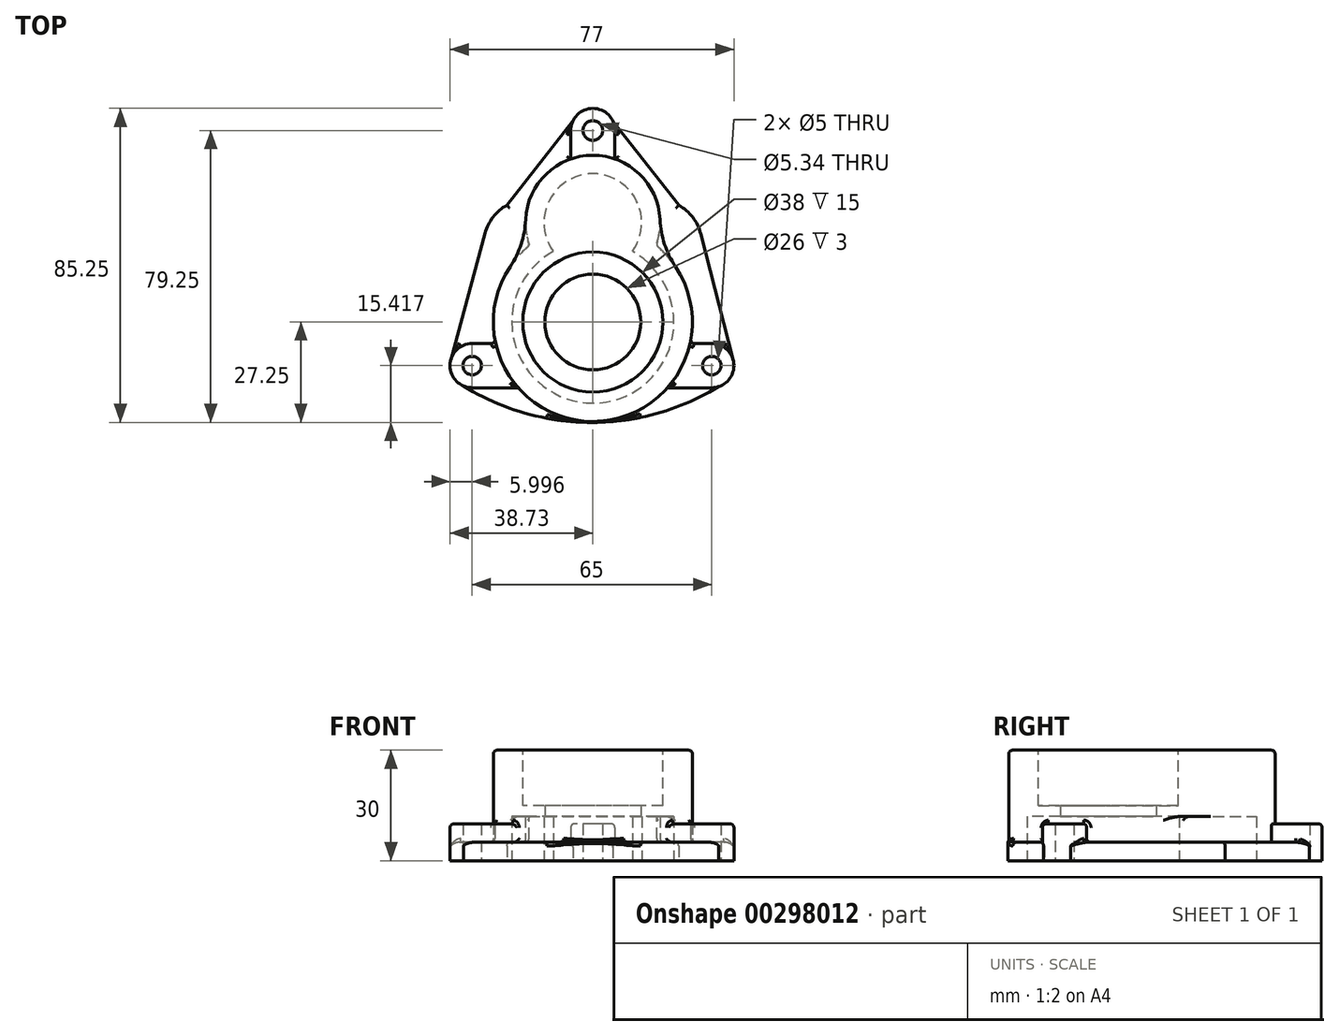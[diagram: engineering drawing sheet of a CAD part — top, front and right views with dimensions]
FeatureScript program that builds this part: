
annotation { "Feature Type Name" : "Feature", "Feature Type Description" : "" }
export const myFeature = defineFeature(function(context is Context, id is Id, definition is map)
    precondition{}
    {
        {
            var Q0;
            Q0=qCreatedBy(makeId("Top.planeOp"),FACE);
            var sketch = newSketch(context, id + "F0", { "sketchPlane" : qUnion([Q0])});
            skCircle(sketch, "E0", {"center": v(0, 0) * mm, "radius": 13 * mm});
            skCircle(sketch, "E1", {"center": v(0, 0) * mm, "radius": 22 * mm});
            skCircle(sketch, "E2", {"center": v(0, 0) * mm, "radius": 27 * mm});
            skCircle(sketch, "E3", {"center": v(0, 27) * mm, "radius": 13.26 * mm});
            skArc(sketch, "E4", {"start": v(17.18, 20.83) * mm, "mid": v(0, 45.26) * mm, "end": v(-17.18, 20.83) * mm});
            skCircle(sketch, "E5", {"center": v(0, 52) * mm, "radius": 2.67 * mm});
            skCircle(sketch, "E6", {"center": v(0, 52) * mm, "radius": 6 * mm});
            skLineSegment(sketch, "E7", {"start": v(-6, 52) * mm, "end": v(-6, 44.25) * mm});
            skLineSegment(sketch, "E8", {"start": v(6, 52) * mm, "end": v(6, 44.25) * mm});
            skCircle(sketch, "E9", {"center": v(32.27, -11.83) * mm, "radius": 2.5 * mm});
            skCircle(sketch, "E10", {"center": v(-32.73, -11.83) * mm, "radius": 2.5 * mm});
            skCircle(sketch, "E11", {"center": v(-32.73, -11.83) * mm, "radius": 6 * mm});
            skCircle(sketch, "E12", {"center": v(32.27, -11.83) * mm, "radius": 6 * mm});
            skLineSegment(sketch, "E13", {"start": v(-32.73, -5.83) * mm, "end": v(-26.36, -5.83) * mm});
            skLineSegment(sketch, "E14", {"start": v(-32.73, -17.83) * mm, "end": v(-20.27, -17.83) * mm});
            skLineSegment(sketch, "E15", {"start": v(32.27, -5.83) * mm, "end": v(26.36, -5.83) * mm});
            skLineSegment(sketch, "E16", {"start": v(32.27, -17.83) * mm, "end": v(20.27, -17.83) * mm});
            skArc(sketch, "E17", {"start": v(-0.52, 13.75) * mm, "mid": v(-0.33, 13.37) * mm, "end": v(-0.12, 13) * mm});
            skArc(sketch, "E18.trimOffspring", {"start": v(-0.1, 13) * mm, "mid": v(0, 13.37) * mm, "end": v(0.09, 13.74) * mm});
            skArc(sketch, "E19", {"start": v(-35.1, -17.35) * mm, "mid": v(-0.52, -27.25) * mm, "end": v(34.11, -17.54) * mm});
            skArc(sketch, "E20", {"start": v(-23.28, 31.74) * mm, "mid": v(-27.04, 28.51) * mm, "end": v(-29.25, 24.08) * mm});
            skArc(sketch, "E21", {"start": v(29.3, 23.93) * mm, "mid": v(27.1, 28.45) * mm, "end": v(23.28, 31.74) * mm});
            skLineSegment(sketch, "E22", {"start": v(5.4, 54.6) * mm, "end": v(23.28, 31.74) * mm});
            skLineSegment(sketch, "E23", {"start": v(-38.52, -10.23) * mm, "end": v(-29.25, 24.08) * mm});
            skLineSegment(sketch, "E24", {"start": v(38.05, -10.23) * mm, "end": v(29.25, 24.08) * mm});
            skLineSegment(sketch, "E25", {"start": v(-23.28, 31.74) * mm, "end": v(-5.4, 54.6) * mm});
            skCircle(sketch, "E26", {"center": v(0, 0) * mm, "radius": 19 * mm});
            skSolve(sketch);
        }
        {
            var Q0;
            {var subQ0=sQuery(id+"F0.wireOp",EDGE,"E4");var subQ1=sQuery(id+"F0.wireOp",EDGE,"E2");var subQ2=makeQuery(id+"F0.imprint","INTERSECT",VERTEX,{"disambiguationData":[OD(0.0)],"derivedFrom":[subQ1,subQ0]});Q0=makeQuery(id+"F0.imprint","IMPRINT",FACE,{"disambiguationData":[TD([[makeQuery(id+"F0.imprint","IMPRINT",EDGE,{"disambiguationData":[TD([[subQ2,-1.0]])],"derivedFrom":subQ1}),-1.0]])]});}
            var Q1;
            {var subQ0=sQuery(id+"F0.wireOp",EDGE,"E3");var subQ1=sQuery(id+"F0.wireOp",EDGE,"E2");var subQ2=makeQuery(id+"F0.imprint","INTERSECT",VERTEX,{"disambiguationData":[OD(0.0)],"derivedFrom":[subQ1,subQ0]});Q1=makeQuery(id+"F0.imprint","IMPRINT",FACE,{"disambiguationData":[TD([[makeQuery(id+"F0.imprint","IMPRINT",EDGE,{"disambiguationData":[TD([[subQ2,-1.0]])],"derivedFrom":subQ1}),-1.0]])]});}
            var Q2;
            {var subQ0=sQuery(id+"F0.wireOp",EDGE,"E3");var subQ1=sQuery(id+"F0.wireOp",EDGE,"E1");var subQ2=makeQuery(id+"F0.imprint","INTERSECT",VERTEX,{"disambiguationData":[OD(0.0)],"derivedFrom":[subQ1,subQ0]});Q2=makeQuery(id+"F0.imprint","IMPRINT",FACE,{"disambiguationData":[TD([[makeQuery(id+"F0.imprint","IMPRINT",EDGE,{"disambiguationData":[TD([[subQ2,1.0]])],"derivedFrom":subQ1}),-1.0]])]});}
            var Q3;
            {var subQ0=sQuery(id+"F0.wireOp",EDGE,"E3");var subQ1=sQuery(id+"F0.wireOp",EDGE,"E1");var subQ2=makeQuery(id+"F0.imprint","INTERSECT",VERTEX,{"disambiguationData":[OD(0.0)],"derivedFrom":[subQ1,subQ0]});Q3=makeQuery(id+"F0.imprint","IMPRINT",FACE,{"disambiguationData":[TD([[makeQuery(id+"F0.imprint","IMPRINT",EDGE,{"disambiguationData":[TD([[subQ2,1.0]])],"derivedFrom":subQ1}),1.0]])]});}
            var Q4;
            {var subQ5=sQuery(id+"F0.wireOp",EDGE,"E3");var subQ7=sQuery(id+"F0.wireOp",EDGE,"E1");var subQ8=makeQuery(id+"F0.imprint","INTERSECT",VERTEX,{"disambiguationData":[OD(0.0)],"derivedFrom":[subQ7,subQ5]});Q4=makeQuery(id+"F0.imprint","IMPRINT",FACE,{"disambiguationData":[TD([[makeQuery(id+"F0.imprint","IMPRINT",EDGE,{"disambiguationData":[TD([[subQ8,-1.0]])],"derivedFrom":subQ7}),-1.0]])]});}
            var Q5;
            {var subQ0=sQuery(id+"F0.wireOp",EDGE,"E17");Q5=makeQuery(id+"F0.imprint","IMPRINT",FACE,{"disambiguationData":[TD([[makeQuery(id+"F0.imprint","IMPRINT",EDGE,{"derivedFrom":subQ0}),-1.0]])]});}
            var Q6;
            {var subQ0=sQuery(id+"F0.wireOp",EDGE,"E0");var subQ1=makeQuery(id+"F0.imprint","INTERSECT",VERTEX,{"derivedFrom":[subQ0,sQuery(id+"F0.wireOp",EDGE,"E17")]});Q6=makeQuery(id+"F0.imprint","IMPRINT",FACE,{"disambiguationData":[TD([[makeQuery(id+"F0.imprint","IMPRINT",EDGE,{"disambiguationData":[TD([[subQ1,1.0]])],"derivedFrom":subQ0}),1.0]])]});}
            var Q7;
            {var subQ0=sQuery(id+"F0.wireOp",EDGE,"E18.trimOffspring");Q7=makeQuery(id+"F0.imprint","IMPRINT",FACE,{"disambiguationData":[TD([[makeQuery(id+"F0.imprint","IMPRINT",EDGE,{"derivedFrom":subQ0}),-1.0]])]});}
            var Q8;
            {var subQ5=sQuery(id+"F0.wireOp",EDGE,"E3");var subQ7=sQuery(id+"F0.wireOp",EDGE,"E1");var subQ9=makeQuery(id+"F0.imprint","INTERSECT",VERTEX,{"disambiguationData":[OD(1.0)],"derivedFrom":[subQ7,subQ5]});Q8=makeQuery(id+"F0.imprint","IMPRINT",FACE,{"disambiguationData":[TD([[makeQuery(id+"F0.imprint","IMPRINT",EDGE,{"disambiguationData":[TD([[subQ9,1.0]])],"derivedFrom":subQ7}),-1.0]])]});}
            var Q9;
            {var subQ0=sQuery(id+"F0.wireOp",EDGE,"EhhgxzOm-Avof-nGiS-FMLo-8e5eDJ9eCd3E");var subQ1=sQuery(id+"F0.wireOp",EDGE,"E0");var subQ2=makeQuery(id+"F0.imprint","INTERSECT",VERTEX,{"disambiguationData":[OD(0.0)],"derivedFrom":[subQ1,subQ0]});Q9=makeQuery(id+"F0.imprint","IMPRINT",FACE,{"disambiguationData":[TD([[makeQuery(id+"F0.imprint","IMPRINT",EDGE,{"disambiguationData":[TD([[subQ2,-1.0]])],"derivedFrom":subQ1}),-1.0]])]});}
            var Q10;
            {var subQ2=sQuery(id+"F0.wireOp",EDGE,"EhhgxzOm-Avof-nGiS-FMLo-8e5eDJ9eCd3E");var subQ6=sQuery(id+"F0.wireOp",EDGE,"E1");var subQ7=makeQuery(id+"F0.imprint","INTERSECT",VERTEX,{"disambiguationData":[OD(0.0)],"derivedFrom":[subQ6,subQ2]});Q10=makeQuery(id+"F0.imprint","IMPRINT",FACE,{"disambiguationData":[TD([[makeQuery(id+"F0.imprint","IMPRINT",EDGE,{"disambiguationData":[TD([[subQ7,-1.0]])],"derivedFrom":subQ6}),-1.0]])]});}
            var Q11;
            {var subQ0=sQuery(id+"F0.wireOp",EDGE,"EhhgxzOm-Avof-nGiS-FMLo-8e5eDJ9eCd3E");var subQ1=sQuery(id+"F0.wireOp",EDGE,"E0");var subQ2=makeQuery(id+"F0.imprint","INTERSECT",VERTEX,{"disambiguationData":[OD(0.0)],"derivedFrom":[subQ1,subQ0]});Q11=makeQuery(id+"F0.imprint","IMPRINT",FACE,{"disambiguationData":[TD([[makeQuery(id+"F0.imprint","IMPRINT",EDGE,{"disambiguationData":[TD([[subQ2,-1.0]])],"derivedFrom":subQ1}),1.0]])]});}
            var Q12;
            {var subQ0=sQuery(id+"F0.wireOp",EDGE,"E3");var subQ1=makeQuery(id+"F0.imprint","INTERSECT",VERTEX,{"derivedFrom":[subQ0,sQuery(id+"F0.wireOp",EDGE,"E17")]});Q12=makeQuery(id+"F0.imprint","IMPRINT",FACE,{"disambiguationData":[TD([[makeQuery(id+"F0.imprint","IMPRINT",EDGE,{"disambiguationData":[TD([[subQ1,1.0]])],"derivedFrom":subQ0}),1.0]])]});}
            var Q13;
            {var subQ0=sQuery(id+"F0.wireOp",EDGE,"E3");var subQ1=sQuery(id+"F0.wireOp",EDGE,"E1");var subQ2=makeQuery(id+"F0.imprint","INTERSECT",VERTEX,{"disambiguationData":[OD(1.0)],"derivedFrom":[subQ1,subQ0]});Q13=makeQuery(id+"F0.imprint","IMPRINT",FACE,{"disambiguationData":[TD([[makeQuery(id+"F0.imprint","IMPRINT",EDGE,{"disambiguationData":[TD([[subQ2,1.0]])],"derivedFrom":subQ1}),1.0]])]});}
            var Q14;
            {var subQ0=sQuery(id+"F0.wireOp",EDGE,"E3");var subQ1=sQuery(id+"F0.wireOp",EDGE,"E1");var subQ2=makeQuery(id+"F0.imprint","INTERSECT",VERTEX,{"disambiguationData":[OD(0.0)],"derivedFrom":[subQ1,subQ0]});Q14=makeQuery(id+"F0.imprint","IMPRINT",FACE,{"disambiguationData":[TD([[makeQuery(id+"F0.imprint","IMPRINT",EDGE,{"disambiguationData":[TD([[subQ2,-1.0]])],"derivedFrom":subQ1}),1.0]])]});}
            var Q15;
            {var subQ0=sQuery(id+"F0.wireOp",EDGE,"EhhgxzOm-Avof-nGiS-FMLo-8e5eDJ9eCd3E");var subQ1=sQuery(id+"F0.wireOp",EDGE,"E1");var subQ2=makeQuery(id+"F0.imprint","INTERSECT",VERTEX,{"disambiguationData":[OD(0.0)],"derivedFrom":[subQ1,subQ0]});Q15=makeQuery(id+"F0.imprint","IMPRINT",FACE,{"disambiguationData":[TD([[makeQuery(id+"F0.imprint","IMPRINT",EDGE,{"disambiguationData":[TD([[subQ2,-1.0]])],"derivedFrom":subQ1}),1.0]])]});}
            extrude(context, id + "F1", {"entities" : qUnion([Q0, Q1, Q2, Q3, Q4, Q5, Q6, Q7, Q8, Q9, Q10, Q11, Q12, Q13, Q14, Q15]), "depth" : 30 * mm});
        }
        {
            var Q0;
            {var subQ0=sQuery(id+"F0.wireOp",EDGE,"E4");var subQ1=sQuery(id+"F0.wireOp",EDGE,"E2");Q0=makeQuery(id+"F1.opExtrude","SWEPT_EDGE",EDGE,{"disambiguationData":[OSD([subQ1,subQ0]),TDD([makeQuery(id+"F0.imprint","INTERSECT",VERTEX,{"disambiguationData":[OD(1.0)],"derivedFrom":[subQ1,subQ0]})])]});}
            var Q1;
            {var subQ0=sQuery(id+"F0.wireOp",EDGE,"E4");var subQ1=sQuery(id+"F0.wireOp",EDGE,"E2");Q1=makeQuery(id+"F1.opExtrude","SWEPT_EDGE",EDGE,{"disambiguationData":[OSD([subQ1,subQ0]),TDD([makeQuery(id+"F0.imprint","INTERSECT",VERTEX,{"disambiguationData":[OD(0.0)],"derivedFrom":[subQ1,subQ0]})])]});}
            fillet(context, id + "F2", {"entities" : qUnion([Q0, Q1]), "radius" : 25 * mm, "tangentPropagation" : true, "allowEdgeOverflow" : false});
        }
        {
            var Q0;
            {var subQ0=sQuery(id+"F0.wireOp",EDGE,"E14");Q0=makeQuery(id+"F0.imprint","IMPRINT",FACE,{"disambiguationData":[TD([[makeQuery(id+"F0.imprint","IMPRINT",EDGE,{"derivedFrom":subQ0}),1.0]])]});}
            var Q1;
            {var subQ0=sQuery(id+"F0.wireOp",EDGE,"E13");Q1=makeQuery(id+"F0.imprint","IMPRINT",FACE,{"disambiguationData":[TD([[makeQuery(id+"F0.imprint","IMPRINT",EDGE,{"derivedFrom":subQ0}),-1.0]])]});}
            var Q2;
            Q2=makeQuery(id+"F0.imprint","IMPRINT",FACE,{"disambiguationData":[TD([[makeQuery(id+"F0.imprint","IMPRINT",EDGE,{"derivedFrom":sQuery(id+"F0.wireOp",EDGE,"E10")}),-1.0]])]});
            var Q3;
            {var subQ0=sQuery(id+"F0.wireOp",EDGE,"E16");Q3=makeQuery(id+"F0.imprint","IMPRINT",FACE,{"disambiguationData":[TD([[makeQuery(id+"F0.imprint","IMPRINT",EDGE,{"derivedFrom":subQ0}),-1.0]])]});}
            var Q4;
            {var subQ0=sQuery(id+"F0.wireOp",EDGE,"E15");Q4=makeQuery(id+"F0.imprint","IMPRINT",FACE,{"disambiguationData":[TD([[makeQuery(id+"F0.imprint","IMPRINT",EDGE,{"derivedFrom":subQ0}),1.0]])]});}
            var Q5;
            Q5=makeQuery(id+"F0.imprint","IMPRINT",FACE,{"disambiguationData":[TD([[makeQuery(id+"F0.imprint","IMPRINT",EDGE,{"derivedFrom":sQuery(id+"F0.wireOp",EDGE,"E9")}),-1.0]])]});
            var Q6;
            Q6=makeQuery(id+"F0.imprint","IMPRINT",FACE,{"disambiguationData":[TD([[makeQuery(id+"F0.imprint","IMPRINT",EDGE,{"derivedFrom":sQuery(id+"F0.wireOp",EDGE,"E5")}),-1.0]])]});
            var Q7;
            {var subQ0=sQuery(id+"F0.wireOp",EDGE,"E7");Q7=makeQuery(id+"F0.imprint","IMPRINT",FACE,{"disambiguationData":[TD([[makeQuery(id+"F0.imprint","IMPRINT",EDGE,{"derivedFrom":subQ0}),1.0]])]});}
            var Q8;
            {var subQ0=sQuery(id+"F0.wireOp",EDGE,"E7");Q8=makeQuery(id+"F0.imprint","IMPRINT",FACE,{"disambiguationData":[TD([[makeQuery(id+"F0.imprint","IMPRINT",EDGE,{"derivedFrom":subQ0}),-1.0]])]});}
            var Q9;
            {var subQ0=sQuery(id+"F0.wireOp",EDGE,"E8");Q9=makeQuery(id+"F0.imprint","IMPRINT",FACE,{"disambiguationData":[TD([[makeQuery(id+"F0.imprint","IMPRINT",EDGE,{"derivedFrom":subQ0}),1.0]])]});}
            var Q10;
            {var subQ0=sQuery(id+"F0.wireOp",EDGE,"E14");Q10=makeQuery(id+"F0.imprint","IMPRINT",FACE,{"disambiguationData":[TD([[makeQuery(id+"F0.imprint","IMPRINT",EDGE,{"derivedFrom":subQ0}),-1.0]])]});}
            extrude(context, id + "F3", {"entities" : qUnion([Q0, Q1, Q2, Q3, Q4, Q5, Q6, Q7, Q8, Q9, Q10]), "operationType" : NewBodyOperationType.ADD, "depth" : 10 * mm});
        }
        {
            var Q0;
            {var subQ0=sQuery(id+"F0.wireOp",EDGE,"E7");Q0=makeQuery(id+"F0.imprint","IMPRINT",FACE,{"disambiguationData":[TD([[makeQuery(id+"F0.imprint","IMPRINT",EDGE,{"derivedFrom":subQ0}),-1.0]])]});}
            var Q1;
            {var subQ0=sQuery(id+"F0.wireOp",EDGE,"E8");Q1=makeQuery(id+"F0.imprint","IMPRINT",FACE,{"disambiguationData":[TD([[makeQuery(id+"F0.imprint","IMPRINT",EDGE,{"derivedFrom":subQ0}),1.0]])]});}
            var Q2;
            {var subQ3=sQuery(id+"F0.wireOp",EDGE,"E14");Q2=makeQuery(id+"F0.imprint","IMPRINT",FACE,{"disambiguationData":[TD([[makeQuery(id+"F0.imprint","IMPRINT",EDGE,{"derivedFrom":subQ3}),-1.0]])]});}
            var Q3;
            {var subQ0=sQuery(id+"F0.wireOp",EDGE,"E3");var subQ1=sQuery(id+"F0.wireOp",EDGE,"E2");var subQ2=makeQuery(id+"F0.imprint","INTERSECT",VERTEX,{"disambiguationData":[OD(0.0)],"derivedFrom":[subQ1,subQ0]});Q3=makeQuery(id+"F0.imprint","IMPRINT",FACE,{"disambiguationData":[TD([[makeQuery(id+"F0.imprint","IMPRINT",EDGE,{"disambiguationData":[TD([[subQ2,-1.0]])],"derivedFrom":subQ1}),-1.0]])]});}
            var Q4;
            {var subQ0=sQuery(id+"F0.wireOp",EDGE,"E3");var subQ1=sQuery(id+"F0.wireOp",EDGE,"E1");var subQ2=makeQuery(id+"F0.imprint","INTERSECT",VERTEX,{"disambiguationData":[OD(0.0)],"derivedFrom":[subQ1,subQ0]});Q4=makeQuery(id+"F0.imprint","IMPRINT",FACE,{"disambiguationData":[TD([[makeQuery(id+"F0.imprint","IMPRINT",EDGE,{"disambiguationData":[TD([[subQ2,1.0]])],"derivedFrom":subQ1}),-1.0]])]});}
            var Q5;
            {var subQ0=sQuery(id+"F0.wireOp",EDGE,"E3");var subQ1=sQuery(id+"F0.wireOp",EDGE,"E1");var subQ2=makeQuery(id+"F0.imprint","INTERSECT",VERTEX,{"disambiguationData":[OD(0.0)],"derivedFrom":[subQ1,subQ0]});Q5=makeQuery(id+"F0.imprint","IMPRINT",FACE,{"disambiguationData":[TD([[makeQuery(id+"F0.imprint","IMPRINT",EDGE,{"disambiguationData":[TD([[subQ2,1.0]])],"derivedFrom":subQ1}),1.0]])]});}
            var Q6;
            {var subQ0=sQuery(id+"F0.wireOp",EDGE,"E3");var subQ1=makeQuery(id+"F0.imprint","INTERSECT",VERTEX,{"derivedFrom":[subQ0,sQuery(id+"F0.wireOp",EDGE,"E17")]});Q6=makeQuery(id+"F0.imprint","IMPRINT",FACE,{"disambiguationData":[TD([[makeQuery(id+"F0.imprint","IMPRINT",EDGE,{"disambiguationData":[TD([[subQ1,1.0]])],"derivedFrom":subQ0}),1.0]])]});}
            var Q7;
            {var subQ5=sQuery(id+"F0.wireOp",EDGE,"E18.trimOffspring");Q7=makeQuery(id+"F0.imprint","IMPRINT",FACE,{"disambiguationData":[TD([[makeQuery(id+"F0.imprint","IMPRINT",EDGE,{"derivedFrom":subQ5}),-1.0]])]});}
            var Q8;
            {var subQ0=sQuery(id+"F0.wireOp",EDGE,"E0");var subQ1=makeQuery(id+"F0.imprint","INTERSECT",VERTEX,{"derivedFrom":[subQ0,sQuery(id+"F0.wireOp",EDGE,"E17")]});Q8=makeQuery(id+"F0.imprint","IMPRINT",FACE,{"disambiguationData":[TD([[makeQuery(id+"F0.imprint","IMPRINT",EDGE,{"disambiguationData":[TD([[subQ1,1.0]])],"derivedFrom":subQ0}),1.0]])]});}
            var Q9;
            {var subQ5=sQuery(id+"F0.wireOp",EDGE,"E17");Q9=makeQuery(id+"F0.imprint","IMPRINT",FACE,{"disambiguationData":[TD([[makeQuery(id+"F0.imprint","IMPRINT",EDGE,{"derivedFrom":subQ5}),-1.0]])]});}
            var Q10;
            {var subQ0=sQuery(id+"F0.wireOp",EDGE,"EhhgxzOm-Avof-nGiS-FMLo-8e5eDJ9eCd3E");var subQ1=sQuery(id+"F0.wireOp",EDGE,"E0");var subQ2=makeQuery(id+"F0.imprint","INTERSECT",VERTEX,{"disambiguationData":[OD(0.0)],"derivedFrom":[subQ1,subQ0]});Q10=makeQuery(id+"F0.imprint","IMPRINT",FACE,{"disambiguationData":[TD([[makeQuery(id+"F0.imprint","IMPRINT",EDGE,{"disambiguationData":[TD([[subQ2,-1.0]])],"derivedFrom":subQ1}),-1.0]])]});}
            var Q11;
            {var subQ0=sQuery(id+"F0.wireOp",EDGE,"EhhgxzOm-Avof-nGiS-FMLo-8e5eDJ9eCd3E");var subQ1=sQuery(id+"F0.wireOp",EDGE,"E0");var subQ2=makeQuery(id+"F0.imprint","INTERSECT",VERTEX,{"disambiguationData":[OD(0.0)],"derivedFrom":[subQ1,subQ0]});Q11=makeQuery(id+"F0.imprint","IMPRINT",FACE,{"disambiguationData":[TD([[makeQuery(id+"F0.imprint","IMPRINT",EDGE,{"disambiguationData":[TD([[subQ2,-1.0]])],"derivedFrom":subQ1}),1.0]])]});}
            var Q12;
            {var subQ0=sQuery(id+"F0.wireOp",EDGE,"E3");var subQ1=sQuery(id+"F0.wireOp",EDGE,"E1");var subQ2=makeQuery(id+"F0.imprint","INTERSECT",VERTEX,{"disambiguationData":[OD(1.0)],"derivedFrom":[subQ1,subQ0]});Q12=makeQuery(id+"F0.imprint","IMPRINT",FACE,{"disambiguationData":[TD([[makeQuery(id+"F0.imprint","IMPRINT",EDGE,{"disambiguationData":[TD([[subQ2,1.0]])],"derivedFrom":subQ1}),1.0]])]});}
            var Q13;
            {var subQ0=sQuery(id+"F0.wireOp",EDGE,"E3");var subQ1=sQuery(id+"F0.wireOp",EDGE,"E1");var subQ2=makeQuery(id+"F0.imprint","INTERSECT",VERTEX,{"disambiguationData":[OD(0.0)],"derivedFrom":[subQ1,subQ0]});Q13=makeQuery(id+"F0.imprint","IMPRINT",FACE,{"disambiguationData":[TD([[makeQuery(id+"F0.imprint","IMPRINT",EDGE,{"disambiguationData":[TD([[subQ2,-1.0]])],"derivedFrom":subQ1}),1.0]])]});}
            var Q14;
            {var subQ0=sQuery(id+"F0.wireOp",EDGE,"EhhgxzOm-Avof-nGiS-FMLo-8e5eDJ9eCd3E");var subQ1=sQuery(id+"F0.wireOp",EDGE,"E1");var subQ2=makeQuery(id+"F0.imprint","INTERSECT",VERTEX,{"disambiguationData":[OD(0.0)],"derivedFrom":[subQ1,subQ0]});Q14=makeQuery(id+"F0.imprint","IMPRINT",FACE,{"disambiguationData":[TD([[makeQuery(id+"F0.imprint","IMPRINT",EDGE,{"disambiguationData":[TD([[subQ2,-1.0]])],"derivedFrom":subQ1}),1.0]])]});}
            extrude(context, id + "F4", {"entities" : qUnion([Q0, Q1, Q2, Q3, Q4, Q5, Q6, Q7, Q8, Q9, Q10, Q11, Q12, Q13, Q14]), "operationType" : NewBodyOperationType.REMOVE, "depth" : 12 * mm});
        }
        {
            var Q0;
            {var subQ0=sQuery(id+"F0.wireOp",EDGE,"E7");Q0=makeQuery(id+"F0.imprint","IMPRINT",FACE,{"disambiguationData":[TD([[makeQuery(id+"F0.imprint","IMPRINT",EDGE,{"derivedFrom":subQ0}),-1.0]])]});}
            var Q1;
            {var subQ0=sQuery(id+"F0.wireOp",EDGE,"E8");Q1=makeQuery(id+"F0.imprint","IMPRINT",FACE,{"disambiguationData":[TD([[makeQuery(id+"F0.imprint","IMPRINT",EDGE,{"derivedFrom":subQ0}),1.0]])]});}
            var Q2;
            {var subQ0=sQuery(id+"F0.wireOp",EDGE,"E14");Q2=makeQuery(id+"F0.imprint","IMPRINT",FACE,{"disambiguationData":[TD([[makeQuery(id+"F0.imprint","IMPRINT",EDGE,{"derivedFrom":subQ0}),-1.0]])]});}
            extrude(context, id + "F5", {"entities" : qUnion([Q0, Q1, Q2]), "operationType" : NewBodyOperationType.ADD, "depth" : 5 * mm});
        }
        {
            var Q0;
            Q0=makeQuery(id+"F1.opExtrude","CAP_FACE",FACE,{"disambiguationData":[OSD([sQuery(id+"F0.wireOp",EDGE,"E0"),sQuery(id+"F0.wireOp",EDGE,"E2"),sQuery(id+"F0.wireOp",EDGE,"E3"),sQuery(id+"F0.wireOp",EDGE,"E4"),sQuery(id+"F0.wireOp",EDGE,"E17"),sQuery(id+"F0.wireOp",EDGE,"E18.trimOffspring")])],"isStart":false});
            var sketch = newSketch(context, id + "F6", { "sketchPlane" : qUnion([Q0])});
            skCircle(sketch, "E27.0", {"center": v(0, 0) * mm, "radius": 19 * mm});
            skSolve(sketch);
        }
        {
            var Q0;
            Q0 = qSketchRegion(id + "F6", true);
            extrude(context, id + "F7", {"entities" : qUnion([Q0]), "operationType" : NewBodyOperationType.REMOVE, "oppositeDirection" : true, "depth" : 15 * mm});
        }
        {
            var Q0;
            {var subQ0=sQuery(id+"F0.wireOp",EDGE,"E0");var subQ1=makeQuery(id+"F0.imprint","INTERSECT",VERTEX,{"derivedFrom":[subQ0,sQuery(id+"F0.wireOp",EDGE,"E17")]});Q0=makeQuery(id+"F0.imprint","IMPRINT",FACE,{"disambiguationData":[TD([[makeQuery(id+"F0.imprint","IMPRINT",EDGE,{"disambiguationData":[TD([[subQ1,1.0]])],"derivedFrom":subQ0}),1.0]])]});}
            extrude(context, id + "F8", {"entities" : qUnion([Q0]), "operationType" : NewBodyOperationType.REMOVE, "endBound" : BoundingType.THROUGH_ALL, "depth" : 25 * mm});
        }
        {
            var Q0;
            Q0=makeQuery(id+"F5.opExtrude","CAP_FACE",FACE,{"disambiguationData":[OSD([sQuery(id+"F0.wireOp",EDGE,"E2"),sQuery(id+"F0.wireOp",EDGE,"E4"),sQuery(id+"F0.wireOp",EDGE,"E6"),sQuery(id+"F0.wireOp",EDGE,"E7"),sQuery(id+"F0.wireOp",EDGE,"E11"),sQuery(id+"F0.wireOp",EDGE,"E13"),sQuery(id+"F0.wireOp",EDGE,"E20"),sQuery(id+"F0.wireOp",EDGE,"E23"),sQuery(id+"F0.wireOp",EDGE,"E25")])],"isStart":false});
            var Q1;
            Q1=makeQuery(id+"F5.opExtrude","CAP_FACE",FACE,{"disambiguationData":[OSD([sQuery(id+"F0.wireOp",EDGE,"E2"),sQuery(id+"F0.wireOp",EDGE,"E4"),sQuery(id+"F0.wireOp",EDGE,"E6"),sQuery(id+"F0.wireOp",EDGE,"E8"),sQuery(id+"F0.wireOp",EDGE,"E12"),sQuery(id+"F0.wireOp",EDGE,"E15"),sQuery(id+"F0.wireOp",EDGE,"E21"),sQuery(id+"F0.wireOp",EDGE,"E22"),sQuery(id+"F0.wireOp",EDGE,"E24")])],"isStart":false});
            var Q2;
            {var subQ0=sQuery(id+"F0.wireOp",EDGE,"E4");var subQ1=sQuery(id+"F0.wireOp",EDGE,"E2");Q2=makeQuery(id+"F4.boolean.opBoolean","MERGE",FACE,{"derivedFrom":[makeQuery(id+"F1.opExtrude","SWEPT_FACE",FACE,{"disambiguationData":[OSD([subQ1])]}),makeQuery(id+"F4.opExtrude","SWEPT_FACE",FACE,{"disambiguationData":[OSD([subQ1]),TDD([makeQuery(id+"F0.imprint","IMPRINT",EDGE,{"disambiguationData":[TD([[makeQuery(id+"F0.imprint","INTERSECT",VERTEX,{"disambiguationData":[OD(1.0)],"derivedFrom":[subQ1,subQ0]}),-1.0]])],"derivedFrom":subQ1})])]}),makeQuery(id+"F4.opExtrude","SWEPT_FACE",FACE,{"disambiguationData":[OSD([subQ1]),TDD([makeQuery(id+"F0.imprint","IMPRINT",EDGE,{"disambiguationData":[TD([[makeQuery(id+"F0.imprint","INTERSECT",VERTEX,{"derivedFrom":[subQ1,sQuery(id+"F0.wireOp",EDGE,"E14")]}),-1.0]])],"derivedFrom":subQ1})])]}),makeQuery(id+"F4.opExtrude","SWEPT_FACE",FACE,{"disambiguationData":[OSD([subQ1]),TDD([makeQuery(id+"F0.imprint","IMPRINT",EDGE,{"disambiguationData":[TD([[makeQuery(id+"F0.imprint","INTERSECT",VERTEX,{"disambiguationData":[OD(0.0)],"derivedFrom":[subQ1,subQ0]}),1.0]])],"derivedFrom":subQ1})])]})]});}
            var Q3;
            Q3=makeQuery(id+"F4.boolean.opBoolean","INTERSECT",EDGE,{"derivedFrom":[makeQuery(id+"F3.opExtrude","CAP_FACE",FACE,{"disambiguationData":[OSD([sQuery(id+"F0.wireOp",EDGE,"E2"),sQuery(id+"F0.wireOp",EDGE,"E4"),sQuery(id+"F0.wireOp",EDGE,"E5"),sQuery(id+"F0.wireOp",EDGE,"E6"),sQuery(id+"F0.wireOp",EDGE,"E9"),sQuery(id+"F0.wireOp",EDGE,"E10"),sQuery(id+"F0.wireOp",EDGE,"E11"),sQuery(id+"F0.wireOp",EDGE,"E12"),sQuery(id+"F0.wireOp",EDGE,"E19"),sQuery(id+"F0.wireOp",EDGE,"E20"),sQuery(id+"F0.wireOp",EDGE,"E21"),sQuery(id+"F0.wireOp",EDGE,"E22"),sQuery(id+"F0.wireOp",EDGE,"E23"),sQuery(id+"F0.wireOp",EDGE,"E24"),sQuery(id+"F0.wireOp",EDGE,"E25")])],"isStart":false}),makeQuery(id+"F4.opExtrude","SWEPT_FACE",FACE,{"disambiguationData":[OSD([sQuery(id+"F0.wireOp",EDGE,"E7")])]})]});
            var Q4;
            Q4=makeQuery(id+"F4.boolean.opBoolean","INTERSECT",EDGE,{"derivedFrom":[makeQuery(id+"F3.opExtrude","CAP_FACE",FACE,{"disambiguationData":[OSD([sQuery(id+"F0.wireOp",EDGE,"E2"),sQuery(id+"F0.wireOp",EDGE,"E4"),sQuery(id+"F0.wireOp",EDGE,"E5"),sQuery(id+"F0.wireOp",EDGE,"E6"),sQuery(id+"F0.wireOp",EDGE,"E9"),sQuery(id+"F0.wireOp",EDGE,"E10"),sQuery(id+"F0.wireOp",EDGE,"E11"),sQuery(id+"F0.wireOp",EDGE,"E12"),sQuery(id+"F0.wireOp",EDGE,"E19"),sQuery(id+"F0.wireOp",EDGE,"E20"),sQuery(id+"F0.wireOp",EDGE,"E21"),sQuery(id+"F0.wireOp",EDGE,"E22"),sQuery(id+"F0.wireOp",EDGE,"E23"),sQuery(id+"F0.wireOp",EDGE,"E24"),sQuery(id+"F0.wireOp",EDGE,"E25")])],"isStart":false}),makeQuery(id+"F4.opExtrude","SWEPT_FACE",FACE,{"disambiguationData":[OSD([sQuery(id+"F0.wireOp",EDGE,"E16")])]})]});
            var Q5;
            Q5=makeQuery(id+"F4.boolean.opBoolean","INTERSECT",EDGE,{"derivedFrom":[makeQuery(id+"F3.opExtrude","CAP_FACE",FACE,{"disambiguationData":[OSD([sQuery(id+"F0.wireOp",EDGE,"E2"),sQuery(id+"F0.wireOp",EDGE,"E4"),sQuery(id+"F0.wireOp",EDGE,"E5"),sQuery(id+"F0.wireOp",EDGE,"E6"),sQuery(id+"F0.wireOp",EDGE,"E9"),sQuery(id+"F0.wireOp",EDGE,"E10"),sQuery(id+"F0.wireOp",EDGE,"E11"),sQuery(id+"F0.wireOp",EDGE,"E12"),sQuery(id+"F0.wireOp",EDGE,"E19"),sQuery(id+"F0.wireOp",EDGE,"E20"),sQuery(id+"F0.wireOp",EDGE,"E21"),sQuery(id+"F0.wireOp",EDGE,"E22"),sQuery(id+"F0.wireOp",EDGE,"E23"),sQuery(id+"F0.wireOp",EDGE,"E24"),sQuery(id+"F0.wireOp",EDGE,"E25")])],"isStart":false}),makeQuery(id+"F4.opExtrude","SWEPT_FACE",FACE,{"disambiguationData":[OSD([sQuery(id+"F0.wireOp",EDGE,"E14")])]})]});
            var Q6;
            Q6=makeQuery(id+"F5.opExtrude","CAP_EDGE",EDGE,{"disambiguationData":[OSD([sQuery(id+"F0.wireOp",EDGE,"E14")])],"isStart":false});
            fillet(context, id + "F9", {"entities" : qUnion([Q0, Q1, Q2, Q3, Q4, Q5, Q6]), "radius" : 1 * mm, "tangentPropagation" : true, "allowEdgeOverflow" : false});
        }
        {
            var Q0;
            Q0=makeQuery(id+"F5.opExtrude","CAP_EDGE",EDGE,{"disambiguationData":[OSD([sQuery(id+"F0.wireOp",EDGE,"E19")])],"isStart":false});
            fillet(context, id + "F10", {"entities" : qUnion([Q0]), "radius" : 1 * mm, "tangentPropagation" : true, "allowEdgeOverflow" : false});
        }
    });
